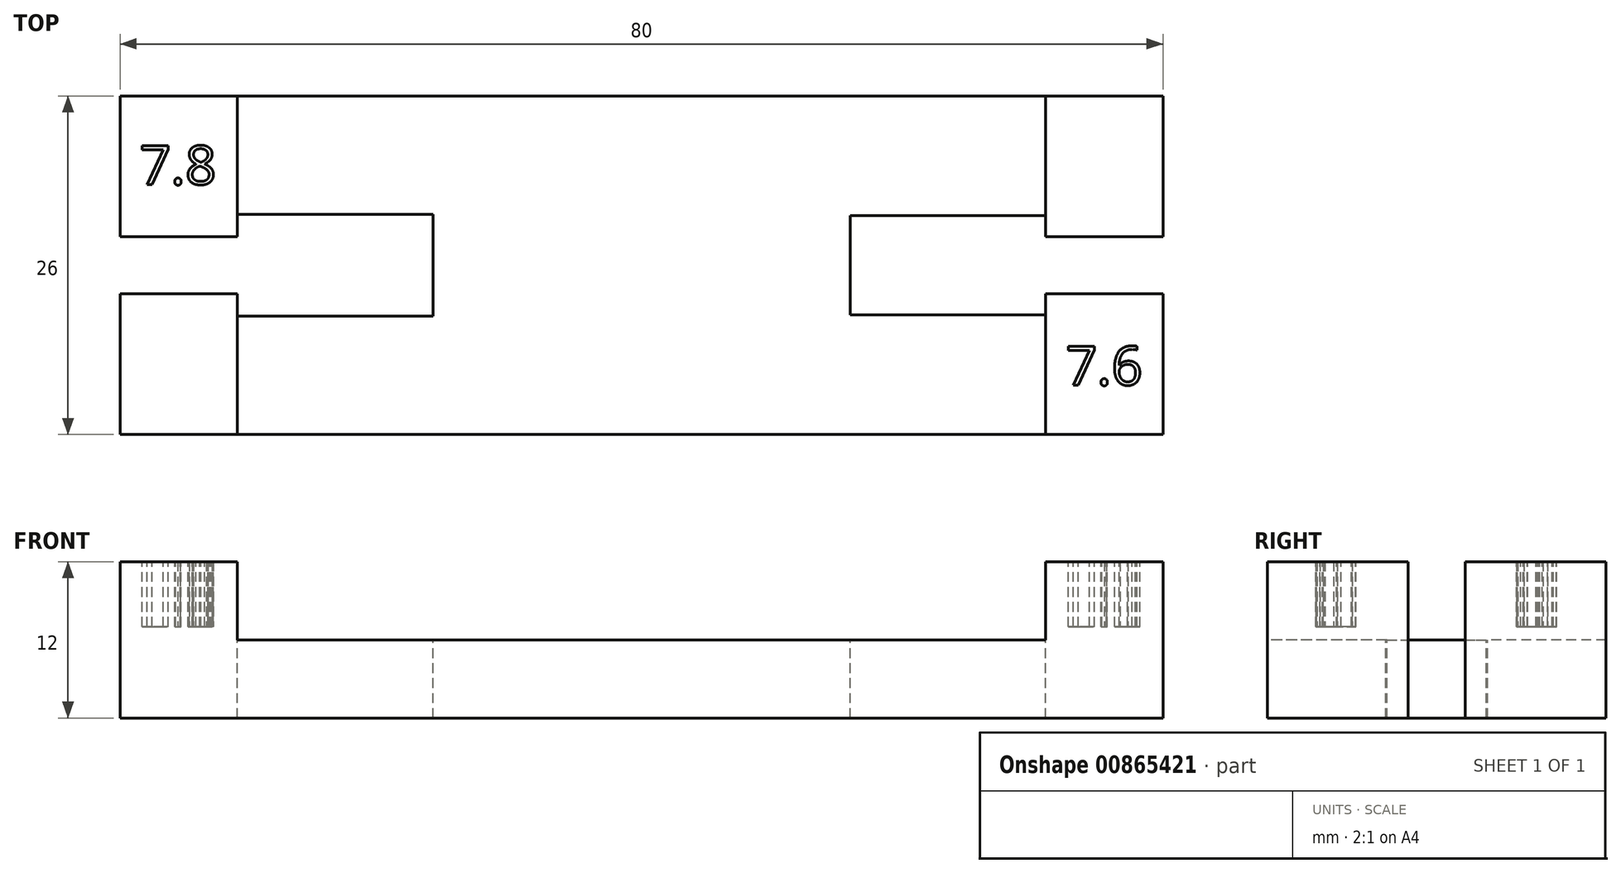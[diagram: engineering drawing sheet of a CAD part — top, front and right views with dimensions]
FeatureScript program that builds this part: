
annotation { "Feature Type Name" : "Feature", "Feature Type Description" : "" }
export const myFeature = defineFeature(function(context is Context, id is Id, definition is map)
    precondition{}
    {
        {
            var Q0;
            Q0=qCreatedBy(makeId("Top.planeOp"),FACE);
            var sketch = newSketch(context, id + "F0", { "sketchPlane" : qUnion([Q0])});
            skLineSegment(sketch, "E0.bottom", {"start": v(40, 13) * mm, "end": v(-40, 13) * mm});
            skLineSegment(sketch, "E0.top", {"start": v(40, -13) * mm, "end": v(-40, -13) * mm});
            skLineSegment(sketch, "E0.left", {"start": v(40, 13) * mm, "end": v(40, -13) * mm});
            skLineSegment(sketch, "E0.right", {"start": v(-40, 13) * mm, "end": v(-40, -13) * mm});
            skPoint(sketch, "E0.middle", {"position": v(0, 0) * mm});
            skLineSegment(sketch, "E1.bottom", {"start": v(-40, -2.2) * mm, "end": v(-16, -2.2) * mm});
            skLineSegment(sketch, "E1.top", {"start": v(-40, 2.2) * mm, "end": v(-16, 2.2) * mm});
            skLineSegment(sketch, "E1.left", {"start": v(-40, -2.2) * mm, "end": v(-40, 2.2) * mm});
            skLineSegment(sketch, "E1.right", {"start": v(-16, -2.2) * mm, "end": v(-16, 2.2) * mm});
            skLineSegment(sketch, "E2.bottom", {"start": v(40, -2.2) * mm, "end": v(16, -2.2) * mm});
            skLineSegment(sketch, "E2.top", {"start": v(40, 2.2) * mm, "end": v(16, 2.2) * mm});
            skLineSegment(sketch, "E2.left", {"start": v(40, -2.2) * mm, "end": v(40, 2.2) * mm});
            skLineSegment(sketch, "E2.right", {"start": v(16, -2.2) * mm, "end": v(16, 2.2) * mm});
            skSolve(sketch);
        }
        {
            var Q0;
            {var subQ6=sQuery(id+"F0.wireOp",EDGE,"E0.bottom");Q0=makeQuery(id+"F0.imprint","IMPRINT",FACE,{"disambiguationData":[TD([[makeQuery(id+"F0.imprint","IMPRINT",EDGE,{"derivedFrom":subQ6}),1.0]])]});}
            extrude(context, id + "F1", {"entities" : qUnion([Q0]), "depth" : 12 * mm, "offsetDistance" : 25 * mm});
        }
        {
            var Q0;
            Q0=makeQuery(id+"F1.opExtrude","CAP_FACE",FACE,{"disambiguationData":[OSD([sQuery(id+"F0.wireOp",EDGE,"E0.bottom"),sQuery(id+"F0.wireOp",EDGE,"E0.top"),sQuery(id+"F0.wireOp",EDGE,"E0.left"),sQuery(id+"F0.wireOp",EDGE,"E0.right"),sQuery(id+"F0.wireOp",EDGE,"E1.bottom"),sQuery(id+"F0.wireOp",EDGE,"E1.top"),sQuery(id+"F0.wireOp",EDGE,"E1.right"),sQuery(id+"F0.wireOp",EDGE,"E2.bottom"),sQuery(id+"F0.wireOp",EDGE,"E2.top"),sQuery(id+"F0.wireOp",EDGE,"E2.right")])],"isStart":false});
            var sketch = newSketch(context, id + "F2", { "sketchPlane" : qUnion([Q0])});
            skLineSegment(sketch, "E3.bottom", {"start": v(-31, 13) * mm, "end": v(31, 13) * mm});
            skLineSegment(sketch, "E3.top", {"start": v(-31, -13) * mm, "end": v(31, -13) * mm});
            skLineSegment(sketch, "E3.left", {"start": v(-31, 13) * mm, "end": v(-31, -13) * mm});
            skLineSegment(sketch, "E3.right", {"start": v(31, 13) * mm, "end": v(31, -13) * mm});
            skLineSegment(sketch, "E4.bottom", {"start": v(-40, 13) * mm, "end": v(40, 13) * mm});
            skLineSegment(sketch, "E4.top", {"start": v(-40, 8) * mm, "end": v(40, 8) * mm});
            skLineSegment(sketch, "E4.left", {"start": v(-40, 13) * mm, "end": v(-40, 8) * mm});
            skLineSegment(sketch, "E4.right", {"start": v(40, 13) * mm, "end": v(40, 8) * mm});
            skLineSegment(sketch, "E5.bottom", {"start": v(40, -13) * mm, "end": v(-40, -13) * mm});
            skLineSegment(sketch, "E5.top", {"start": v(40, -8) * mm, "end": v(-40, -8) * mm});
            skLineSegment(sketch, "E5.left", {"start": v(40, -13) * mm, "end": v(40, -8) * mm});
            skLineSegment(sketch, "E5.right", {"start": v(-40, -13) * mm, "end": v(-40, -8) * mm});
            skSolve(sketch);
        }
        {
            var Q0;
            {var subQ0=sQuery(id+"F2.wireOp",EDGE,"E4.bottom");var subQ1=sQuery(id+"F2.wireOp",EDGE,"E3.left");var subQ2=makeQuery(id+"F2.imprint","INTERSECT",VERTEX,{"derivedFrom":[subQ1,subQ0]});Q0=makeQuery(id+"F2.imprint","IMPRINT",FACE,{"disambiguationData":[TD([[makeQuery(id+"F2.imprint","IMPRINT",EDGE,{"disambiguationData":[TD([[subQ2,-1.0]])],"derivedFrom":subQ1}),1.0]])]});}
            var Q1;
            {var subQ0=makeQuery(id+"F1.opExtrude","CAP_EDGE",EDGE,{"disambiguationData":[OSD([sQuery(id+"F0.wireOp",EDGE,"E1.right")])],"isStart":false});Q1=makeQuery(id+"F2.imprint","IMPRINT",FACE,{"disambiguationData":[TD([[makeQuery(id+"F2.imprint","IMPRINT",EDGE,{"derivedFrom":subQ0}),-1.0]])]});}
            var Q2;
            {var subQ0=sQuery(id+"F2.wireOp",EDGE,"E5.bottom");var subQ1=sQuery(id+"F2.wireOp",EDGE,"E3.left");var subQ2=makeQuery(id+"F2.imprint","INTERSECT",VERTEX,{"derivedFrom":[subQ1,subQ0]});Q2=makeQuery(id+"F2.imprint","IMPRINT",FACE,{"disambiguationData":[TD([[makeQuery(id+"F2.imprint","IMPRINT",EDGE,{"disambiguationData":[TD([[subQ2,1.0]])],"derivedFrom":subQ1}),1.0]])]});}
            extrude(context, id + "F3", {"entities" : qUnion([Q0, Q1, Q2]), "operationType" : NewBodyOperationType.REMOVE, "oppositeDirection" : true, "depth" : 6 * mm, "offsetDistance" : 25 * mm});
        }
        {
            var Q0;
            Q0=makeQuery(id+"F3.boolean.opBoolean","COPY",FACE,{"derivedFrom":makeQuery(id+"F3.opExtrude","CAP_FACE",FACE,{"disambiguationData":[OSD([sQuery(id+"F0.wireOp",EDGE,"E1.bottom"),sQuery(id+"F0.wireOp",EDGE,"E1.top"),sQuery(id+"F0.wireOp",EDGE,"E1.right"),sQuery(id+"F0.wireOp",EDGE,"E2.bottom"),sQuery(id+"F0.wireOp",EDGE,"E2.top"),sQuery(id+"F0.wireOp",EDGE,"E2.right"),sQuery(id+"F2.wireOp",EDGE,"E3.left"),sQuery(id+"F2.wireOp",EDGE,"E3.right"),sQuery(id+"F2.wireOp",EDGE,"E4.bottom"),sQuery(id+"F2.wireOp",EDGE,"E4.top"),sQuery(id+"F2.wireOp",EDGE,"E4.left"),sQuery(id+"F2.wireOp",EDGE,"E4.right"),sQuery(id+"F2.wireOp",EDGE,"E5.bottom"),sQuery(id+"F2.wireOp",EDGE,"E5.top"),sQuery(id+"F2.wireOp",EDGE,"E5.left"),sQuery(id+"F2.wireOp",EDGE,"E5.right")])],"isStart":false})});
            var sketch = newSketch(context, id + "F4", { "sketchPlane" : qUnion([Q0])});
            skLineSegment(sketch, "E6.bottom", {"start": v(-16, 3.9) * mm, "end": v(-31, 3.9) * mm});
            skLineSegment(sketch, "E6.top", {"start": v(-16, -3.9) * mm, "end": v(-31, -3.9) * mm});
            skLineSegment(sketch, "E6.left", {"start": v(-16, 3.9) * mm, "end": v(-16, -3.9) * mm});
            skLineSegment(sketch, "E6.right", {"start": v(-31, 3.9) * mm, "end": v(-31, -3.9) * mm});
            skLineSegment(sketch, "E7.bottom", {"start": v(16, 3.8) * mm, "end": v(31, 3.8) * mm});
            skLineSegment(sketch, "E7.top", {"start": v(16, -3.8) * mm, "end": v(31, -3.8) * mm});
            skLineSegment(sketch, "E7.left", {"start": v(16, 3.8) * mm, "end": v(16, -3.8) * mm});
            skLineSegment(sketch, "E7.right", {"start": v(31, 3.8) * mm, "end": v(31, -3.8) * mm});
            skSolve(sketch);
        }
        {
            var Q0;
            {var subQ0=sQuery(id+"F4.wireOp",EDGE,"E6.bottom");Q0=makeQuery(id+"F4.imprint","IMPRINT",FACE,{"disambiguationData":[TD([[makeQuery(id+"F4.imprint","IMPRINT",EDGE,{"derivedFrom":subQ0}),1.0]])]});}
            var Q1;
            {var subQ0=sQuery(id+"F4.wireOp",EDGE,"E6.top");Q1=makeQuery(id+"F4.imprint","IMPRINT",FACE,{"disambiguationData":[TD([[makeQuery(id+"F4.imprint","IMPRINT",EDGE,{"derivedFrom":subQ0}),-1.0]])]});}
            var Q2;
            {var subQ0=sQuery(id+"F4.wireOp",EDGE,"E7.bottom");Q2=makeQuery(id+"F4.imprint","IMPRINT",FACE,{"disambiguationData":[TD([[makeQuery(id+"F4.imprint","IMPRINT",EDGE,{"derivedFrom":subQ0}),-1.0]])]});}
            var Q3;
            {var subQ0=sQuery(id+"F4.wireOp",EDGE,"E7.top");Q3=makeQuery(id+"F4.imprint","IMPRINT",FACE,{"disambiguationData":[TD([[makeQuery(id+"F4.imprint","IMPRINT",EDGE,{"derivedFrom":subQ0}),1.0]])]});}
            extrude(context, id + "F5", {"entities" : qUnion([Q0, Q1, Q2, Q3]), "operationType" : NewBodyOperationType.REMOVE, "oppositeDirection" : true, "depth" : 25 * mm, "offsetDistance" : 25 * mm});
        }
        {
            var Q0;
            {var subQ0=sQuery(id+"F0.wireOp",EDGE,"E0.bottom");var subQ1=sQuery(id+"F0.wireOp",EDGE,"E0.right");var subQ2=sQuery(id+"F0.wireOp",EDGE,"E1.top");Q0=makeQuery(id+"F3.boolean.opBoolean","SPLIT",FACE,{"disambiguationData":[TD([makeQuery(id+"F1.opExtrude","SWEPT_FACE",FACE,{"disambiguationData":[OSD([subQ2])]})])],"derivedFrom":makeQuery(id+"F1.opExtrude","CAP_FACE",FACE,{"disambiguationData":[OSD([subQ0,sQuery(id+"F0.wireOp",EDGE,"E0.top"),sQuery(id+"F0.wireOp",EDGE,"E0.left"),subQ1,sQuery(id+"F0.wireOp",EDGE,"E1.bottom"),subQ2,sQuery(id+"F0.wireOp",EDGE,"E1.right"),sQuery(id+"F0.wireOp",EDGE,"E2.bottom"),sQuery(id+"F0.wireOp",EDGE,"E2.top"),sQuery(id+"F0.wireOp",EDGE,"E2.right")])],"isStart":false})});}
            var sketch = newSketch(context, id + "F6", { "sketchPlane" : qUnion([Q0])});
            skText(sketch, "E8", { "text": "7.8", "fontName": "OpenSans-Regular.ttf"});
            const initialGuessF6  = {"E8": [-0.0385, 0.0062, 1, 0, 0.003]};
            skSetInitialGuess(sketch, initialGuessF6);
            skSolve(sketch);
        }
        {
            var Q0;
            Q0 = qSketchRegion(id + "F6", true);
            extrude(context, id + "F7", {"entities" : qUnion([Q0]), "operationType" : NewBodyOperationType.REMOVE, "oppositeDirection" : true, "depth" : 5 * mm, "offsetDistance" : 25 * mm});
        }
        {
            var Q0;
            {var subQ0=sQuery(id+"F0.wireOp",EDGE,"E0.top");var subQ3=sQuery(id+"F0.wireOp",EDGE,"E2.bottom");var subQ4=sQuery(id+"F0.wireOp",EDGE,"E0.left");Q0=makeQuery(id+"F3.boolean.opBoolean","SPLIT",FACE,{"disambiguationData":[TD([makeQuery(id+"F1.opExtrude","SWEPT_FACE",FACE,{"disambiguationData":[OSD([subQ3])]})])],"derivedFrom":makeQuery(id+"F1.opExtrude","CAP_FACE",FACE,{"disambiguationData":[OSD([sQuery(id+"F0.wireOp",EDGE,"E0.bottom"),subQ0,subQ4,sQuery(id+"F0.wireOp",EDGE,"E0.right"),sQuery(id+"F0.wireOp",EDGE,"E1.bottom"),sQuery(id+"F0.wireOp",EDGE,"E1.top"),sQuery(id+"F0.wireOp",EDGE,"E1.right"),subQ3,sQuery(id+"F0.wireOp",EDGE,"E2.top"),sQuery(id+"F0.wireOp",EDGE,"E2.right")])],"isStart":false})});}
            var sketch = newSketch(context, id + "F8", { "sketchPlane" : qUnion([Q0])});
            skText(sketch, "E9", { "text": "7.6", "fontName": "OpenSans-Regular.ttf"});
            const initialGuessF8  = {"E9": [0.03256, -0.0092, 1, 0, 0.003]};
            skSetInitialGuess(sketch, initialGuessF8);
            skSolve(sketch);
        }
        {
            var Q0;
            Q0 = qSketchRegion(id + "F8", true);
            extrude(context, id + "F9", {"entities" : qUnion([Q0]), "operationType" : NewBodyOperationType.REMOVE, "oppositeDirection" : true, "depth" : 5 * mm, "offsetDistance" : 25 * mm});
        }
    });
